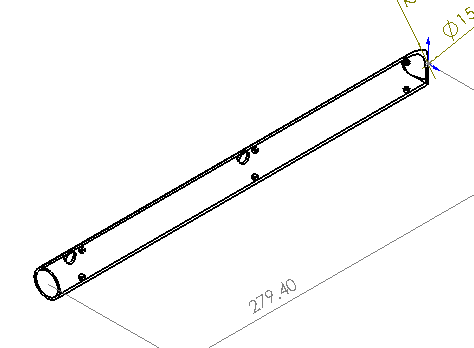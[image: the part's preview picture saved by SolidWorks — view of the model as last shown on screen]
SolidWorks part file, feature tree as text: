
SOLIDWORKS PART (.sldprt)
format: sldprt  version: not decoded by parser v0  size: 228,352 bytes
history: native  units: mm
features: sketch x4, cut_extrude x3, material x1, extrude x1 + 1 further entry (+14 scaffold rows collapsed)
feature tree (24):
  scaffold x14  (default folders/planes/origin — collapsed)
  material  "Material <not specified>"
  "Annotations"  RD1=18.72mm RD4=15.98mm RD2=279.4mm
  sketch  "Sketch1"  dims[D1=7.875mm]
  extrude  "Extrude1"  Depth=279.4mm
  sketch  "Sketch2"  dims[D1=~8.980256mm]
  cut_extrude  "Cut-Extrude1"  [1 undecoded]
  sketch  "Sketch3"  dims[D1=3.175mm]
  cut_extrude  "Cut-Extrude2"  [1 undecoded]
  sketch  "Sketch4"  dims[D1=~4.490128mm]
  cut_extrude  "Cut-Extrude3"  [1 undecoded]
decode coverage: 5 of 8 modeling features carry decoded parameters; 1 rows unclassified (native names shown)
note: ~ marks probable driven/reference dimensions
note: 3 parameter values undecoded
summary: no parameter record found for 3 features
note: suppression state not decoded; provenance and decode notes live in map.json
